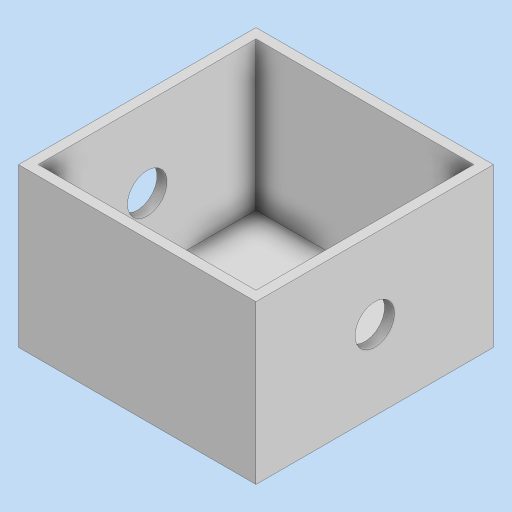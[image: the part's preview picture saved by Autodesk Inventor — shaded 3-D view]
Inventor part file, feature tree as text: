
AUTODESK INVENTOR PART (.ipt)
format: ipt  version: 2024 (Build 280153000, 153)  size: 126,464 bytes
history: native  units: in
note: dims shown in document units (in); Inventor stores cm internally (conversion verified against a paired STEP export)
features: extrude x3, sketch x3, projected_geometry x2
ambient origin geometry x8: Origin, YZ Plane, XZ Plane, XY Plane, X Axis, Y Axis, Z Axis, Center Point
bodies: Solid1 (feature_tree)
feature tree (8):
  extrude  "Extrusion1"  Depth=3.0in
  extrude  "Extrusion2"  Depth=0.125in
  extrude  "Extrusion3"  Depth=0.125in
  sketch  "Sketch1"  dims[d0=3.0in d1=3.0in]
  sketch  "Sketch2"  dims[d2=2.0in d3=0.0in d4=0.125in]
  projected_geometry  "Projected Loop1"
  sketch  "Sketch3"  dims[d5=0.125in d6=0.125in d7=0.125in d8=1.875in d9=0.0in d10=0.5in d11=0.0in d12=0.0in]
  projected_geometry  "Projected Loop2"
